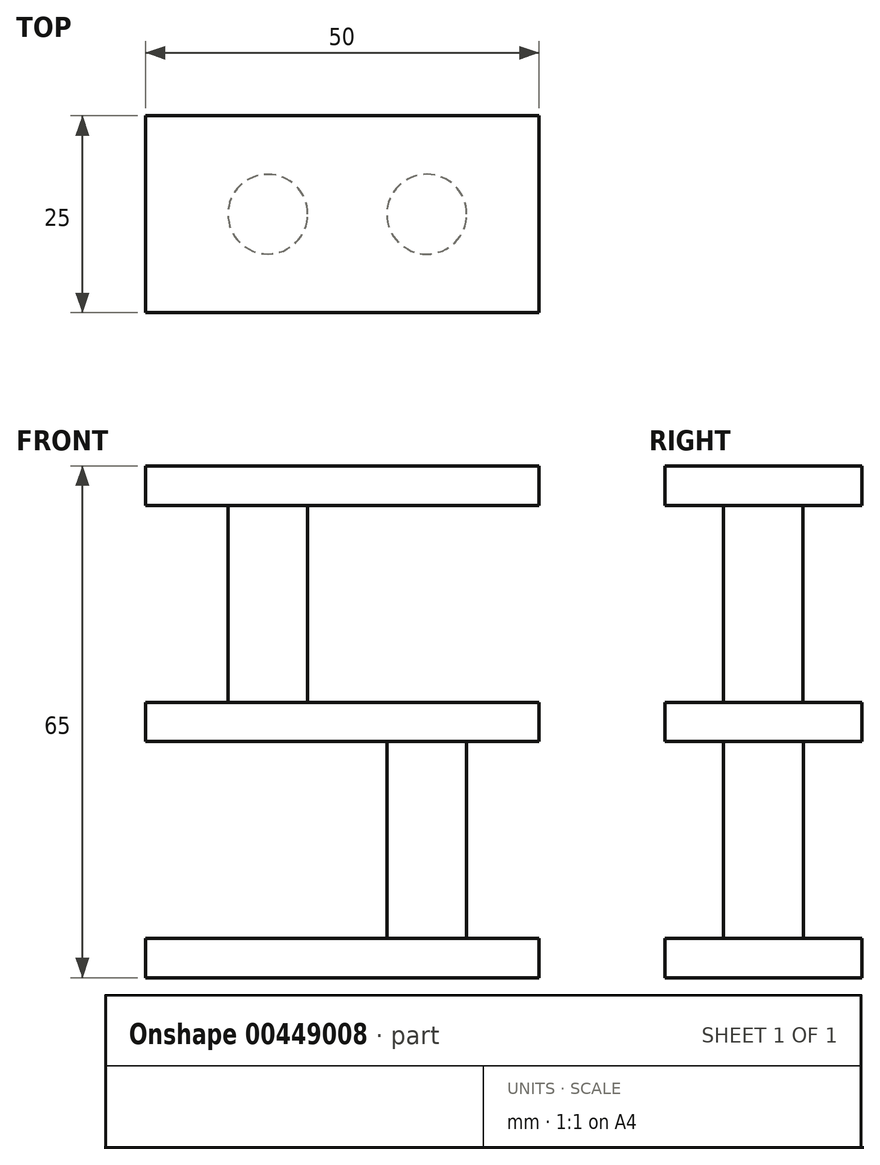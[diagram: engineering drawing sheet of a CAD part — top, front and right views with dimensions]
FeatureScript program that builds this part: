
annotation { "Feature Type Name" : "Feature", "Feature Type Description" : "" }
export const myFeature = defineFeature(function(context is Context, id is Id, definition is map)
    precondition{}
    {
        {
            var Q0;
            Q0=qCreatedBy(makeId("Front.planeOp"),FACE);
            var sketch = newSketch(context, id + "F0", { "sketchPlane" : qUnion([Q0])});
            skLineSegment(sketch, "E0.bottom", {"start": v(0, -32.5) * mm, "end": v(50, -32.5) * mm});
            skLineSegment(sketch, "E0.top", {"start": v(0, -27.5) * mm, "end": v(50, -27.5) * mm});
            skLineSegment(sketch, "E0.left", {"start": v(0, -32.5) * mm, "end": v(0, -27.5) * mm});
            skLineSegment(sketch, "E0.right", {"start": v(50, -32.5) * mm, "end": v(50, -27.5) * mm});
            skLineSegment(sketch, "E1.bottom", {"start": v(0, -27.5) * mm, "end": v(5, -27.5) * mm});
            skLineSegment(sketch, "E1.top", {"start": v(0, -2.5) * mm, "end": v(5, -2.5) * mm});
            skLineSegment(sketch, "E1.left", {"start": v(0, -27.5) * mm, "end": v(0, -2.5) * mm});
            skLineSegment(sketch, "E1.right", {"start": v(5, -27.5) * mm, "end": v(5, -2.5) * mm});
            skLineSegment(sketch, "E2.bottom", {"start": v(0, -2.5) * mm, "end": v(50, -2.5) * mm});
            skLineSegment(sketch, "E2.top", {"start": v(0, 2.5) * mm, "end": v(50, 2.5) * mm});
            skLineSegment(sketch, "E2.left", {"start": v(0, -2.5) * mm, "end": v(0, 2.5) * mm});
            skLineSegment(sketch, "E2.right", {"start": v(50, -2.5) * mm, "end": v(50, 2.5) * mm});
            skLineSegment(sketch, "E3.bottom", {"start": v(0, 2.5) * mm, "end": v(5, 2.5) * mm});
            skLineSegment(sketch, "E3.top", {"start": v(0, 27.5) * mm, "end": v(5, 27.5) * mm});
            skLineSegment(sketch, "E3.left", {"start": v(0, 2.5) * mm, "end": v(0, 27.5) * mm});
            skLineSegment(sketch, "E3.right", {"start": v(5, 2.5) * mm, "end": v(5, 27.5) * mm});
            skLineSegment(sketch, "E4.bottom", {"start": v(0, 27.5) * mm, "end": v(50, 27.5) * mm});
            skLineSegment(sketch, "E4.top", {"start": v(0, 32.5) * mm, "end": v(50, 32.5) * mm});
            skLineSegment(sketch, "E4.left", {"start": v(0, 27.5) * mm, "end": v(0, 32.5) * mm});
            skLineSegment(sketch, "E4.right", {"start": v(50, 27.5) * mm, "end": v(50, 32.5) * mm});
            skPoint(sketch, "E5", {"position": v(0, 0) * mm});
            skSolve(sketch);
        }
        {
            var Q0;
            Q0=makeQuery(id+"F0.imprint","IMPRINT",FACE,{"disambiguationData":[TD([[makeQuery(id+"F0.imprint","IMPRINT",EDGE,{"derivedFrom":sQuery(id+"F0.wireOp",EDGE,"E0.bottom")}),1.0]])]});
            extrude(context, id + "F1", {"entities" : qUnion([Q0]), "depth" : 25 * mm});
        }
        {
            var Q0;
            Q0=makeQuery(id+"F0.imprint","IMPRINT",FACE,{"disambiguationData":[TD([[makeQuery(id+"F0.imprint","IMPRINT",EDGE,{"derivedFrom":sQuery(id+"F0.wireOp",EDGE,"E2.top")}),-1.0]])]});
            var Q1;
            Q1=makeQuery(id+"F1.opExtrude","CAP_FACE",FACE,{"disambiguationData":[OSD([sQuery(id+"F0.wireOp",EDGE,"E0.bottom"),sQuery(id+"F0.wireOp",EDGE,"E0.top"),sQuery(id+"F0.wireOp",EDGE,"E0.left"),sQuery(id+"F0.wireOp",EDGE,"E0.right"),sQuery(id+"F0.wireOp",EDGE,"E1.left"),sQuery(id+"F0.wireOp",EDGE,"E1.right"),sQuery(id+"F0.wireOp",EDGE,"E2.bottom")])],"isStart":false});
            extrude(context, id + "F2", {"entities" : qUnion([Q0]), "endBound" : BoundingType.UP_TO_SURFACE, "endBoundEntityFace" : qUnion([Q1]), "depth" : 2 * mm});
        }
        {
            var Q0;
            Q0=makeQuery(id+"F0.imprint","IMPRINT",FACE,{"disambiguationData":[TD([[makeQuery(id+"F0.imprint","IMPRINT",EDGE,{"derivedFrom":sQuery(id+"F0.wireOp",EDGE,"E4.top")}),-1.0]])]});
            var Q1;
            Q1=makeQuery(id+"F1.opExtrude","CAP_FACE",FACE,{"disambiguationData":[OSD([sQuery(id+"F0.wireOp",EDGE,"E0.bottom"),sQuery(id+"F0.wireOp",EDGE,"E0.top"),sQuery(id+"F0.wireOp",EDGE,"E0.left"),sQuery(id+"F0.wireOp",EDGE,"E0.right"),sQuery(id+"F0.wireOp",EDGE,"E1.left"),sQuery(id+"F0.wireOp",EDGE,"E1.right"),sQuery(id+"F0.wireOp",EDGE,"E2.bottom")])],"isStart":false});
            extrude(context, id + "F3", {"entities" : qUnion([Q0]), "endBound" : BoundingType.UP_TO_SURFACE, "endBoundEntityFace" : qUnion([Q1]), "depth" : 25 * mm});
        }
        {
            var Q0;
            Q0=qCreatedBy(makeId("Top.planeOp"),FACE);
            var sketch = newSketch(context, id + "F4", { "sketchPlane" : qUnion([Q0])});
            skCircle(sketch, "E6", {"center": v(15.55, -12.5) * mm, "radius": 5.06 * mm});
            skCircle(sketch, "E7", {"center": v(35.75, -12.5) * mm, "radius": 5.07 * mm});
            skLineSegment(sketch, "E8.0", {"start": v(0, -25) * mm, "end": v(0, 0) * mm, "construction": true});
            skPoint(sketch, "E9", {"position": v(0, -12.5) * mm});
            skSolve(sketch);
        }
        {
            var Q0;
            Q0=makeQuery(id+"F4.imprint","IMPRINT",FACE,{"disambiguationData":[TD([[makeQuery(id+"F4.imprint","IMPRINT",EDGE,{"derivedFrom":sQuery(id+"F4.wireOp",EDGE,"E7")}),1.0]])]});
            var Q1;
            Q1=makeQuery(id+"F1.opExtrude","SWEPT_BODY",BODY,{"disambiguationData":[OSD([sQuery(id+"F0.wireOp",EDGE,"E0.bottom"),sQuery(id+"F0.wireOp",EDGE,"E0.top"),sQuery(id+"F0.wireOp",EDGE,"E0.left"),sQuery(id+"F0.wireOp",EDGE,"E0.right"),sQuery(id+"F0.wireOp",EDGE,"E1.bottom")])]});
            extrude(context, id + "F5", {"entities" : qUnion([Q0]), "operationType" : NewBodyOperationType.ADD, "endBound" : BoundingType.UP_TO_BODY, "oppositeDirection" : true, "endBoundEntityBody" : qUnion([Q1]), "depth" : 25 * mm});
        }
        {
            var Q0;
            Q0=makeQuery(id+"F4.imprint","IMPRINT",FACE,{"disambiguationData":[TD([[makeQuery(id+"F4.imprint","IMPRINT",EDGE,{"derivedFrom":sQuery(id+"F4.wireOp",EDGE,"E6")}),1.0]])]});
            var Q1;
            Q1=makeQuery(id+"F3.opExtrude","SWEPT_BODY",BODY,{"disambiguationData":[OSD([sQuery(id+"F0.wireOp",EDGE,"E4.bottom"),sQuery(id+"F0.wireOp",EDGE,"E4.top"),sQuery(id+"F0.wireOp",EDGE,"E4.left"),sQuery(id+"F0.wireOp",EDGE,"E4.right")])]});
            extrude(context, id + "F6", {"entities" : qUnion([Q0]), "operationType" : NewBodyOperationType.ADD, "endBound" : BoundingType.UP_TO_BODY, "endBoundEntityBody" : qUnion([Q1]), "depth" : 25 * mm});
        }
    });
